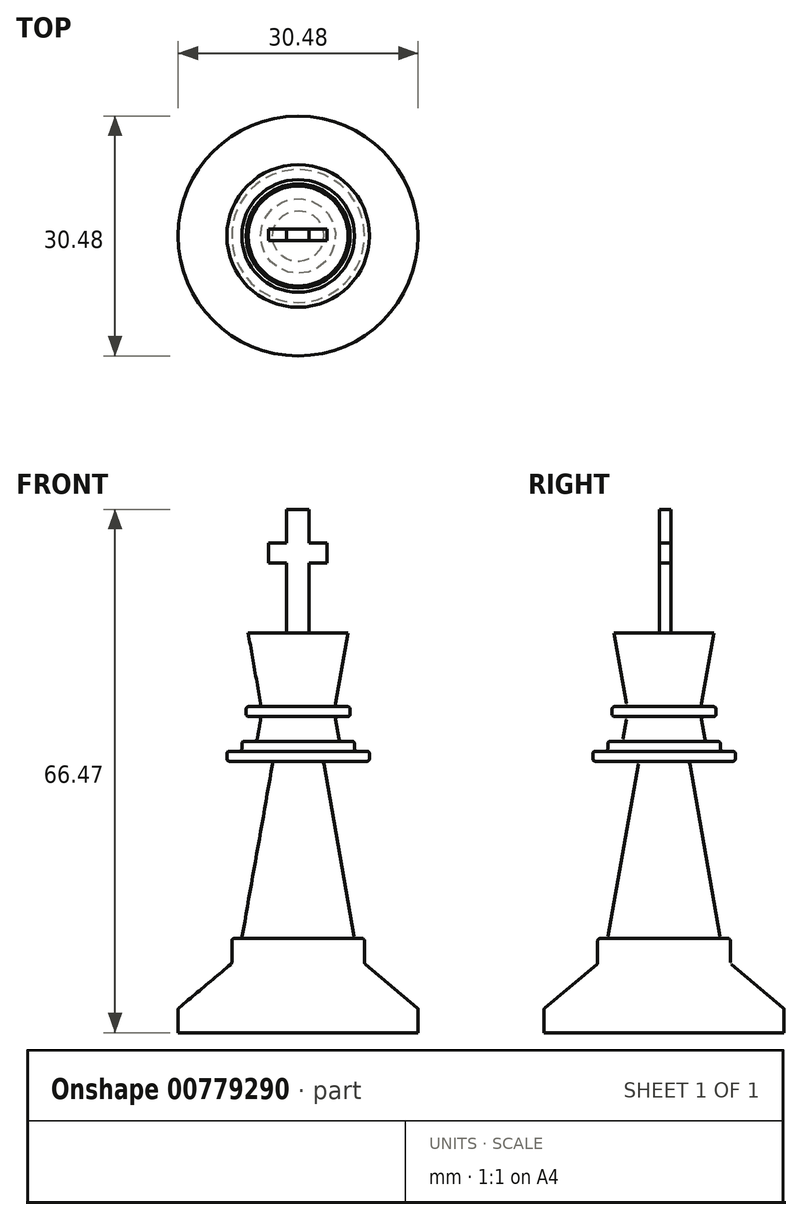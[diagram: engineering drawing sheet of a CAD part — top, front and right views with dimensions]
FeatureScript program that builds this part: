
annotation { "Feature Type Name" : "Feature", "Feature Type Description" : "" }
export const myFeature = defineFeature(function(context is Context, id is Id, definition is map)
    precondition{}
    {
        {
            var Q0;
            Q0=qCreatedBy(makeId("Front.planeOp"),FACE);
            var sketch = newSketch(context, id + "F0", { "sketchPlane" : qUnion([Q0])});
            skLineSegment(sketch, "E0.bottom", {"start": v(0, 0) * mm, "end": v(-15.24, 0) * mm});
            skLineSegment(sketch, "E0.top", {"start": v(0, 50.8) * mm, "end": v(-6.35, 50.8) * mm});
            skLineSegment(sketch, "E0.left", {"start": v(0, 0) * mm, "end": v(0, 50.8) * mm});
            skLineSegment(sketch, "E1", {"start": v(-15.24, 0) * mm, "end": v(-15.24, 2.93) * mm});
            skLineSegment(sketch, "E2", {"start": v(-15.13, 3.18) * mm, "end": v(-8.54, 8.7) * mm});
            skLineSegment(sketch, "E3", {"start": v(-8.43, 8.94) * mm, "end": v(-8.43, 11.65) * mm});
            skLineSegment(sketch, "E4", {"start": v(-8.11, 11.97) * mm, "end": v(-7.43, 11.97) * mm});
            skLineSegment(sketch, "E5", {"start": v(-7.11, 12.23) * mm, "end": v(-3.26, 34.11) * mm});
            skLineSegment(sketch, "E6", {"start": v(-3.57, 34.48) * mm, "end": v(-8.74, 34.48) * mm});
            skLineSegment(sketch, "E7", {"start": v(-9.06, 34.8) * mm, "end": v(-9.06, 35.44) * mm});
            skLineSegment(sketch, "E8", {"start": v(-8.74, 35.75) * mm, "end": v(-7.47, 35.75) * mm});
            skLineSegment(sketch, "E9", {"start": v(-7.15, 36.07) * mm, "end": v(-7.15, 36.7) * mm});
            skLineSegment(sketch, "E10", {"start": v(-6.83, 37.02) * mm, "end": v(-5.51, 37.02) * mm});
            skLineSegment(sketch, "E11", {"start": v(-5.2, 37.29) * mm, "end": v(-4.76, 39.78) * mm});
            skLineSegment(sketch, "E12", {"start": v(-5.07, 40.15) * mm, "end": v(-6.28, 40.15) * mm});
            skLineSegment(sketch, "E13", {"start": v(-6.6, 40.47) * mm, "end": v(-6.6, 41.1) * mm});
            skLineSegment(sketch, "E14", {"start": v(-6.28, 41.42) * mm, "end": v(-5.07, 41.42) * mm});
            skLineSegment(sketch, "E15", {"start": v(-4.76, 41.8) * mm, "end": v(-6.35, 50.8) * mm});
            skPoint(sketch, "E16.visualSharp", {"position": v(-15.24, 3.08) * mm});
            skArc(sketch, "E16.filletArc", {"start": v(-15.13, 3.18) * mm, "mid": v(-15.21, 3.07) * mm, "end": v(-15.24, 2.93) * mm});
            skPoint(sketch, "E17.visualSharp", {"position": v(-8.43, 8.8) * mm});
            skArc(sketch, "E17.filletArc", {"start": v(-8.54, 8.7) * mm, "mid": v(-8.46, 8.8) * mm, "end": v(-8.43, 8.94) * mm});
            skPoint(sketch, "E18.visualSharp", {"position": v(-3.2, 34.48) * mm});
            skArc(sketch, "E18.filletArc", {"start": v(-3.26, 34.11) * mm, "mid": v(-3.33, 34.37) * mm, "end": v(-3.57, 34.48) * mm});
            skPoint(sketch, "E19.visualSharp", {"position": v(-8.43, 11.97) * mm});
            skArc(sketch, "E19.filletArc", {"start": v(-8.11, 11.97) * mm, "mid": v(-8.34, 11.88) * mm, "end": v(-8.43, 11.65) * mm});
            skPoint(sketch, "E20.visualSharp", {"position": v(-7.16, 11.97) * mm});
            skArc(sketch, "E20.filletArc", {"start": v(-7.43, 11.97) * mm, "mid": v(-7.22, 12.04) * mm, "end": v(-7.11, 12.23) * mm});
            skPoint(sketch, "E21.visualSharp", {"position": v(-9.06, 34.48) * mm});
            skArc(sketch, "E21.filletArc", {"start": v(-9.06, 34.8) * mm, "mid": v(-8.96, 34.58) * mm, "end": v(-8.74, 34.48) * mm});
            skPoint(sketch, "E22.visualSharp", {"position": v(-9.06, 35.75) * mm});
            skArc(sketch, "E22.filletArc", {"start": v(-8.74, 35.75) * mm, "mid": v(-8.96, 35.66) * mm, "end": v(-9.06, 35.44) * mm});
            skPoint(sketch, "E23.visualSharp", {"position": v(-7.15, 35.75) * mm});
            skArc(sketch, "E23.filletArc", {"start": v(-7.47, 35.75) * mm, "mid": v(-7.25, 35.85) * mm, "end": v(-7.15, 36.07) * mm});
            skPoint(sketch, "E24.visualSharp", {"position": v(-7.15, 37.02) * mm});
            skArc(sketch, "E24.filletArc", {"start": v(-6.83, 37.02) * mm, "mid": v(-7.06, 36.93) * mm, "end": v(-7.15, 36.7) * mm});
            skPoint(sketch, "E25.visualSharp", {"position": v(-5.25, 37.02) * mm});
            skArc(sketch, "E25.filletArc", {"start": v(-5.51, 37.02) * mm, "mid": v(-5.3, 37.1) * mm, "end": v(-5.2, 37.29) * mm});
            skPoint(sketch, "E26.visualSharp", {"position": v(-4.7, 40.15) * mm});
            skArc(sketch, "E26.filletArc", {"start": v(-4.76, 39.78) * mm, "mid": v(-4.83, 40.04) * mm, "end": v(-5.07, 40.15) * mm});
            skPoint(sketch, "E27.visualSharp", {"position": v(-6.6, 40.15) * mm});
            skArc(sketch, "E27.filletArc", {"start": v(-6.6, 40.47) * mm, "mid": v(-6.5, 40.24) * mm, "end": v(-6.28, 40.15) * mm});
            skPoint(sketch, "E28.visualSharp", {"position": v(-6.6, 41.42) * mm});
            skArc(sketch, "E28.filletArc", {"start": v(-6.28, 41.42) * mm, "mid": v(-6.5, 41.33) * mm, "end": v(-6.6, 41.1) * mm});
            skPoint(sketch, "E29.visualSharp", {"position": v(-4.7, 41.42) * mm});
            skArc(sketch, "E29.filletArc", {"start": v(-5.07, 41.42) * mm, "mid": v(-4.83, 41.53) * mm, "end": v(-4.76, 41.8) * mm});
            skSolve(sketch);
        }
        {
            var Q0;
            Q0=makeQuery(id+"F0.imprint","IMPRINT",FACE,{"disambiguationData":[TD([[makeQuery(id+"F0.imprint","IMPRINT",EDGE,{"derivedFrom":sQuery(id+"F0.wireOp",EDGE,"E0.bottom")}),-1.0]])]});
            var Q1;
            Q1=sQuery(id+"F0.wireOp",EDGE,"E0.left");
            revolve(context, id + "F1", {"surfaceOperationType" : NewSurfaceOperationType.NEW, "entities" : qUnion([Q0]), "axis" : qUnion([Q1]), "revolveType" : RevolveType.FULL});
        }
        {
            var Q0;
            Q0=makeQuery(id+"F1.opRevolve","SWEPT_FACE",FACE,{"disambiguationData":[OSD([sQuery(id+"F0.wireOp",EDGE,"E0.top")])]});
            var sketch = newSketch(context, id + "F2", { "sketchPlane" : qUnion([Q0])});
            skLineSegment(sketch, "E30.bottom", {"start": v(-1.46, 0.9) * mm, "end": v(1.4, 0.9) * mm});
            skLineSegment(sketch, "E30.top", {"start": v(-1.46, -0.59) * mm, "end": v(1.4, -0.59) * mm});
            skLineSegment(sketch, "E30.left", {"start": v(-1.46, 0.9) * mm, "end": v(-1.46, -0.59) * mm});
            skLineSegment(sketch, "E30.right", {"start": v(1.4, 0.9) * mm, "end": v(1.4, -0.59) * mm});
            skSolve(sketch);
        }
        {
            var Q0;
            Q0 = qSketchRegion(id + "F2", true);
            extrude(context, id + "F3", {"entities" : qUnion([Q0]), "operationType" : NewBodyOperationType.ADD, "depth" : 8.9 * mm, "offsetDistance" : 25.4 * mm});
        }
        {
            var Q0;
            Q0=makeQuery(id+"F3.opExtrude","CAP_FACE",FACE,{"disambiguationData":[OSD([sQuery(id+"F2.wireOp",EDGE,"E30.bottom"),sQuery(id+"F2.wireOp",EDGE,"E30.top"),sQuery(id+"F2.wireOp",EDGE,"E30.left"),sQuery(id+"F2.wireOp",EDGE,"E30.right")])],"isStart":false});
            var sketch = newSketch(context, id + "F4", { "sketchPlane" : qUnion([Q0])});
            skLineSegment(sketch, "E31.bottom", {"start": v(-3.75, -0.59) * mm, "end": v(3.7, -0.59) * mm});
            skLineSegment(sketch, "E31.top", {"start": v(-3.75, 0.9) * mm, "end": v(3.7, 0.9) * mm});
            skLineSegment(sketch, "E31.left", {"start": v(-3.75, -0.59) * mm, "end": v(-3.75, 0.9) * mm});
            skLineSegment(sketch, "E31.right", {"start": v(3.7, -0.59) * mm, "end": v(3.7, 0.9) * mm});
            skLineSegment(sketch, "E32", {"start": v(-1.46, -0.59) * mm, "end": v(-1.46, 0.9) * mm});
            skLineSegment(sketch, "E33", {"start": v(1.4, 0.9) * mm, "end": v(1.4, -0.59) * mm});
            skSolve(sketch);
        }
        {
            var Q0;
            {var subQ0=sQuery(id+"F4.wireOp",EDGE,"E32");Q0=makeQuery(id+"F4.imprint","IMPRINT",FACE,{"disambiguationData":[TD([[makeQuery(id+"F4.imprint","IMPRINT",EDGE,{"derivedFrom":subQ0}),1.0]])]});}
            extrude(context, id + "F5", {"entities" : qUnion([Q0]), "operationType" : NewBodyOperationType.ADD, "depth" : 6.78 * mm, "offsetDistance" : 25.4 * mm});
        }
        {
            var Q0;
            {var subQ2=sQuery(id+"F4.wireOp",EDGE,"E31.right");Q0=makeQuery(id+"F4.imprint","IMPRINT",FACE,{"disambiguationData":[TD([[makeQuery(id+"F4.imprint","IMPRINT",EDGE,{"derivedFrom":subQ2}),1.0]])]});}
            var Q1;
            {var subQ2=sQuery(id+"F4.wireOp",EDGE,"E31.left");Q1=makeQuery(id+"F4.imprint","IMPRINT",FACE,{"disambiguationData":[TD([[makeQuery(id+"F4.imprint","IMPRINT",EDGE,{"derivedFrom":subQ2}),-1.0]])]});}
            extrude(context, id + "F6", {"entities" : qUnion([Q0, Q1]), "operationType" : NewBodyOperationType.ADD, "depth" : 2.54 * mm, "offsetDistance" : 25.4 * mm});
        }
        {
            var Q0;
            Q0=makeQuery(id+"F0.imprint","IMPRINT",FACE,{"disambiguationData":[TD([[makeQuery(id+"F0.imprint","IMPRINT",EDGE,{"derivedFrom":sQuery(id+"F0.wireOp",EDGE,"E0.bottom")}),-1.0]])]});
            var Q1;
            Q1=sQuery(id+"F0.wireOp",EDGE,"E0.left");
            revolve(context, id + "F7", {"entities" : qUnion([Q0]), "axis" : qUnion([Q1]), "revolveType" : RevolveType.FULL});
        }
    });
